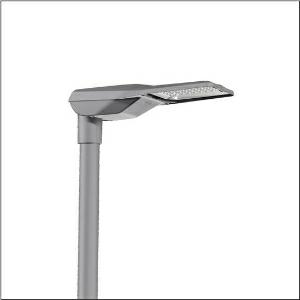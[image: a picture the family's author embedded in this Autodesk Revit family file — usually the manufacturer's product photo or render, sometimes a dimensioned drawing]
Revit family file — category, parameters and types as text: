
# Revit family: streetlight_sl_21_iq_mini___st1_5a_5xe2p31d08gb_fdd6
name_source: partatom
category: Lighting Fixtures
units: mm (PartAtom-declared; Revit-internal decimal feet)

## family parameters
Cut with Voids When Loaded = No
Host = Face
Light Source = No
Part Type = Normal
Room Calculation Point = No
Round Connector Dimension = Use Diameter
Shared = No

## types (1)
- --- (1 x LED, 5580 lm, 37.1 W, 3000K)
    Apparent Load = 37 VA
    CIE Flux Codes = 22 53 95 100 100
    Color Rendering = 70
    Color Temperature = 3000K
    Default Elevation = 1800 mm
    Description = Streetlight SL 21 mini, mast luminaire, primary light control with lens, of PMMA, primary optical cover: cover, of toughened safety glass, transparent, light distribution: ST1.5a, light emission: direct distribution, primary light characteristic: asymmetric, installation type: post-top, side-entry, LED, High Power LED, rated luminous flux: 5.580lm, luminous efficacy: 150lm/W, light colour: 730, colour temperature: 3000K, control gear: ECG iQ, control: Auto-Match, Temp-Guard, Lumen-Switch, Night-Set, Smart-Wire, Light-Fading, Desk-Remote (wireless, voltage-free reading and setting of iQ features in the workshop via application-optimized NFC function/RFID function), optimised constant luminous flux control (CLO 2.0), mains connection: 220..240V, AC, 50/60Hz, start of lifetime: 37W, end of lifetime: 39W, reduction: 18W, luminaire housing, of diecast aluminium, powder-coated, Siteco® metallic grey (DB 702S), corrosivity category C5 according to DIN EN ISO 12944, length: 628mm, width: 235mm, height: 110mm, spigot size: 60/76mm (post-top) and 42/60/76mm (side-entry), mast flange for spigot size: 42mm: 5XC10008XM4, 60mm: 5XC10008XM2, 76/60mm: 5XC10108XM1, protection rating (complete): IP66, insulation class (complete): insulation class II (safety insulation), certification: CE, ENEC, VDE, impact resistance: IK09, permissible operating ambient temperature for outdoor applications: -40..+50°C, standard-compliant lighting for roads and squares, packaging unit: 1 piece

Light Distribution: ST1.5a
    Height = 110 mm
    Lamp = 1 x LED
    Lamp Light Flux = 5580 lm
    Lamp Power = 37.1 W
    Lamp count = 1
    Length = 625 mm
    Luminous efficacy = 150 lm/W
    Manufacturer = Siteco
    ModVariant = No
    Model = 5XE2P31D08GB
    Number of Poles = 1
    OnlyDefault = Yes
    Power Factor = 1
    Product Name = Streetlight SL 21 iQ mini | ST1.5a
    Product group = mast luminaire | pylon top
    ProductGroupID = 6100
    Protection Class = Protection class II
    Protection Degree = IP 66
    RLX_Detail_Level = 1
    RlxData = <blob elided: 95565 chars, md5=080d0b8a>
    Socket = socket
    Standby Power = 0 W
    System Light Flux = 5580 lm
    System Power = 37 W
    Type Comments = factory setting: luminous flux: 100 % | dim-lin: 254 | 385 mA
    Type Image = l_1003519.jpg
    URL = http://relux.com
    VarID = @adj_088675
    Voltage = 0 V
    Weight = 0.00 kg
    Width = 234 mm

## geometry (parser evidence)
native form markers: Blend x4, Sweep x9
no freeform markers — native parametric forms only
